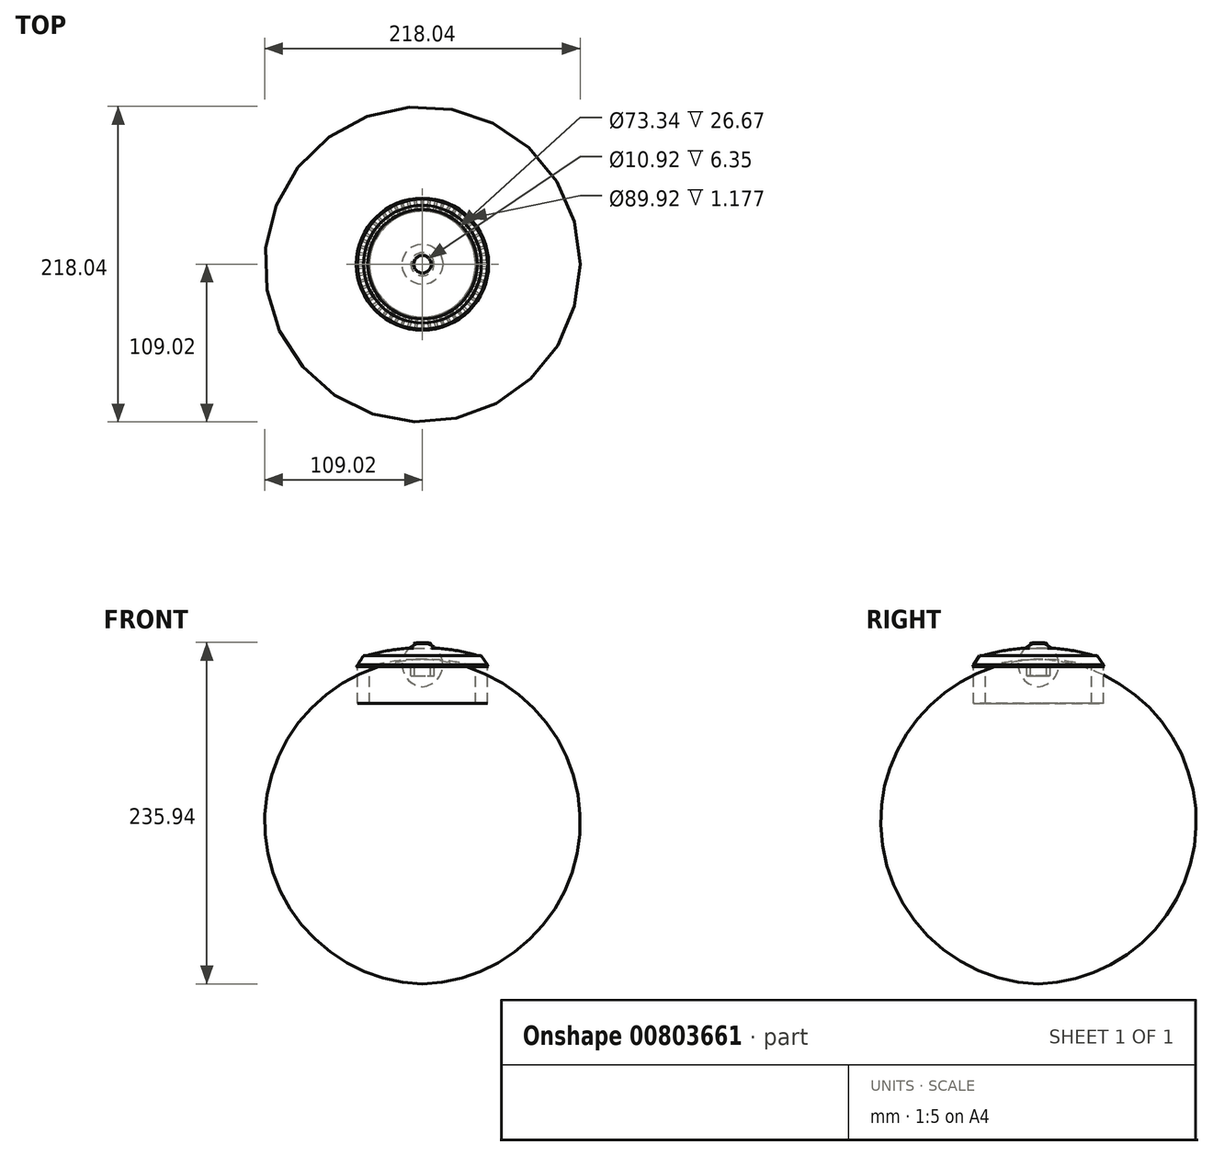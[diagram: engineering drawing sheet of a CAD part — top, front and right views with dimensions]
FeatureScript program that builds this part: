
annotation { "Feature Type Name" : "Feature", "Feature Type Description" : "" }
export const myFeature = defineFeature(function(context is Context, id is Id, definition is map)
    precondition{}
    {
        {
            var Q0;
            Q0=qCreatedBy(makeId("Front.planeOp"),FACE);
            var sketch = newSketch(context, id + "F0", { "sketchPlane" : qUnion([Q0])});
            skLineSegment(sketch, "E0", {"start": v(0, 0) * mm, "end": v(45.72, 0) * mm});
            skLineSegment(sketch, "E1", {"start": v(40.64, 7.87) * mm, "end": v(0, 7.87) * mm});
            skLineSegment(sketch, "E2", {"start": v(0, 0) * mm, "end": v(0, 16.77) * mm});
            skLineSegment(sketch, "E3", {"start": v(0, 16.01) * mm, "end": v(6.1, 16.01) * mm});
            skLineSegment(sketch, "E4", {"start": v(6.1, 16.01) * mm, "end": v(6.1, 12.96) * mm});
            skArc(sketch, "E5", {"start": v(6.1, 16.01) * mm, "mid": v(3.09, 16.7) * mm, "end": v(0, 16.77) * mm});
            skLineSegment(sketch, "E6", {"start": v(39.88, 7.87) * mm, "end": v(37.85, 7.87) * mm});
            skArc(sketch, "E7", {"start": v(37.85, 7.87) * mm, "mid": v(19.13, 11.93) * mm, "end": v(0, 12.96) * mm});
            skLineSegment(sketch, "E8", {"start": v(38.86, 7.87) * mm, "end": v(38.86, 0) * mm, "construction": true});
            skLineSegment(sketch, "E9", {"start": v(45.72, 0) * mm, "end": v(40.64, 7.87) * mm});
            skSolve(sketch);
        }
        {
            var Q0;
            Q0 = qSketchRegion(id + "F0", true);
            var Q1;
            Q1=sQuery(id+"F0.wireOp",EDGE,"E2");
            revolve(context, id + "F1", {"surfaceOperationType" : NewSurfaceOperationType.NEW, "entities" : qUnion([Q0]), "axis" : qUnion([Q1]), "revolveType" : RevolveType.FULL});
        }
        {
            var Q0;
            Q0=makeQuery(id+"F1.opRevolve","SWEPT_FACE",FACE,{"disambiguationData":[OSD([sQuery(id+"F0.wireOp",EDGE,"E0")])]});
            shell(context, id + "F2", {"entities" : qUnion([Q0]), "thickness" : 7.87 * mm});
        }
        {
            var Q0;
            Q0=makeQuery(id+"F1.opRevolve","SWEPT_FACE",FACE,{"disambiguationData":[OSD([sQuery(id+"F0.wireOp",EDGE,"E0")])]});
            var sketch = newSketch(context, id + "F3", { "sketchPlane" : qUnion([Q0])});
            skCircle(sketch, "E10", {"center": v(0, 0) * mm, "radius": 8 * mm});
            skCircle(sketch, "E11", {"center": v(0, 0) * mm, "radius": 5.46 * mm});
            skSolve(sketch);
        }
        {
            var Q0;
            Q0 = qSketchRegion(id + "F3", true);
            extrude(context, id + "F4", {"entities" : qUnion([Q0]), "depth" : 6.35 * mm, "offsetDistance" : 25.4 * mm});
        }
        {
            var Q0;
            Q0=makeQuery(id+"F3.imprint","IMPRINT",FACE,{"disambiguationData":[TD([[makeQuery(id+"F3.imprint","IMPRINT",EDGE,{"derivedFrom":makeQuery(id+"F1.opRevolve","SWEPT_EDGE",EDGE,{"disambiguationData":[OSD([sQuery(id+"F0.wireOp",EDGE,"E0"),sQuery(id+"F0.wireOp",EDGE,"E9")])]})}),1.0]])]});
            var sketch = newSketch(context, id + "F5", { "sketchPlane" : qUnion([Q0])});
            skCircle(sketch, "E12", {"center": v(0, 0) * mm, "radius": 44.96 * mm});
            skSolve(sketch);
        }
        {
            var Q0;
            Q0=makeQuery(id+"F5.imprint","IMPRINT",FACE,{"disambiguationData":[TD([[makeQuery(id+"F5.imprint","IMPRINT",EDGE,{"derivedFrom":sQuery(id+"F5.wireOp",EDGE,"E12")}),1.0]])]});
            extrude(context, id + "F6", {"entities" : qUnion([Q0]), "oppositeDirection" : true, "depth" : 1.27 * mm, "offsetDistance" : 25.4 * mm});
        }
        {
            var Q0;
            Q0=makeQuery(id+"F6.opExtrude","SWEPT_BODY",BODY,{"disambiguationData":[OSD([sQuery(id+"F0.wireOp",EDGE,"E1"),sQuery(id+"F0.wireOp",EDGE,"E6"),sQuery(id+"F0.wireOp",EDGE,"E7"),sQuery(id+"F5.wireOp",EDGE,"E12")])]});
            var Q1;
            Q1=makeQuery(id+"F1.opRevolve","SWEPT_BODY",BODY,{"disambiguationData":[OSD([sQuery(id+"F0.wireOp",EDGE,"E0"),sQuery(id+"F0.wireOp",EDGE,"E1"),sQuery(id+"F0.wireOp",EDGE,"E2"),sQuery(id+"F0.wireOp",EDGE,"E4"),sQuery(id+"F0.wireOp",EDGE,"E5"),sQuery(id+"F0.wireOp",EDGE,"E6"),sQuery(id+"F0.wireOp",EDGE,"E7"),sQuery(id+"F0.wireOp",EDGE,"E9")])]});
            booleanBodies(context, id + "F7", {"operationType" : BooleanOperationType.SUBTRACTION, "tools" : qUnion([Q0]), "targets" : qUnion([Q1])});
        }
        {
            var Q0;
            Q0=makeQuery(id+"F3.imprint","IMPRINT",FACE,{"disambiguationData":[TD([[makeQuery(id+"F3.imprint","IMPRINT",EDGE,{"derivedFrom":makeQuery(id+"F1.opRevolve","SWEPT_EDGE",EDGE,{"disambiguationData":[OSD([sQuery(id+"F0.wireOp",EDGE,"E0"),sQuery(id+"F0.wireOp",EDGE,"E9")])]})}),1.0]])]});
            var sketch = newSketch(context, id + "F8", { "sketchPlane" : qUnion([Q0])});
            skCircle(sketch, "E13.0", {"center": v(0, 0) * mm, "radius": 44.9 * mm});
            skCircle(sketch, "E14.0", {"center": v(0, 0) * mm, "radius": 36.67 * mm});
            skLineSegment(sketch, "E15", {"start": v(0, 36.67) * mm, "end": v(0, 44.9) * mm, "construction": true});
            skLineSegment(sketch, "E16", {"start": v(0.76, 36.66) * mm, "end": v(0.76, 44.9) * mm});
            skLineSegment(sketch, "E17.MirrorCS", {"start": v(-0.76, 36.66) * mm, "end": v(-0.76, 44.9) * mm});
            skSolve(sketch);
        }
        {
            var Q0;
            {var subQ0=sQuery(id+"F8.wireOp",EDGE,"E16");Q0=makeQuery(id+"F8.imprint","IMPRINT",FACE,{"disambiguationData":[TD([[makeQuery(id+"F8.imprint","IMPRINT",EDGE,{"derivedFrom":subQ0}),1.0]])]});}
            extrude(context, id + "F9", {"entities" : qUnion([Q0]), "endBound" : BoundingType.SYMMETRIC, "depth" : 2.54 * mm, "offsetDistance" : 25.4 * mm});
        }
        {
            var Q0;
            Q0=makeQuery(id+"F9.opExtrude","SWEPT_BODY",BODY,{"disambiguationData":[OSD([sQuery(id+"F8.wireOp",EDGE,"E13.0"),sQuery(id+"F8.wireOp",EDGE,"E14.0"),sQuery(id+"F8.wireOp",EDGE,"E16"),sQuery(id+"F8.wireOp",EDGE,"E17.MirrorCS")])]});
            var Q1;
            {var subQ0=sQuery(id+"F0.wireOp",EDGE,"E7");var subQ1=sQuery(id+"F0.wireOp",EDGE,"E6");var subQ2=sQuery(id+"F0.wireOp",EDGE,"E1");Q1=makeQuery(id+"F7.opBoolean","MERGE",EDGE,{"derivedFrom":[makeQuery(id+"F2.opShell","OFFSET_EDGE",EDGE,{"disambiguationData":[OSD([subQ2,subQ1,subQ0])]})],"fromTools":[makeQuery(id+"F6.opExtrude","CAP_EDGE",EDGE,{"disambiguationData":[OSD([subQ2,subQ1,subQ0])],"isStart":true})]});}
            circularPattern(context, id + "F10", {"entities" : qUnion([Q0]), "axis" : qUnion([Q1]), "angle" : 360 * degree, "instanceCount" : 58, "equalSpace" : true});
        }
        {
            var Q0;
            Q0 = qSketchRegion(id + "F8", true);
            extrude(context, id + "F11", {"entities" : qUnion([Q0]), "operationType" : NewBodyOperationType.ADD, "depth" : 25.4 * mm, "offsetDistance" : 25.4 * mm});
        }
    });
